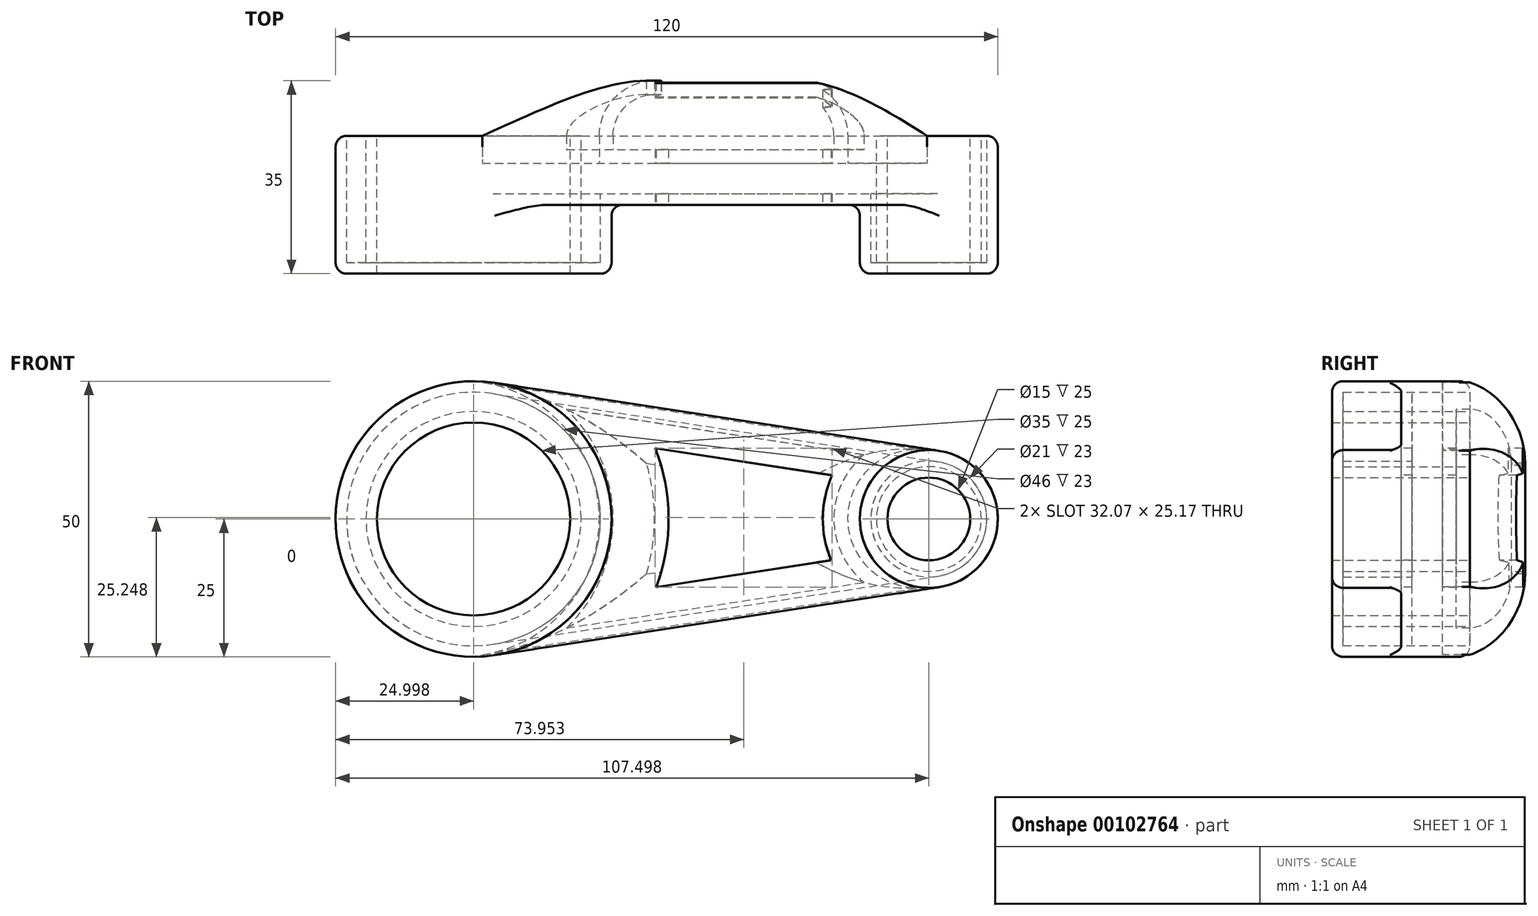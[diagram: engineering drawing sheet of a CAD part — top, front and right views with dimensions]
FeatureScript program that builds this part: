
annotation { "Feature Type Name" : "Feature", "Feature Type Description" : "" }
export const myFeature = defineFeature(function(context is Context, id is Id, definition is map)
    precondition{}
    {
        {
            var Q0;
            Q0=qCreatedBy(makeId("Front.planeOp"),FACE);
            var sketch = newSketch(context, id + "F0", { "sketchPlane" : qUnion([Q0])});
            skLineSegment(sketch, "E0", {"start": v(-63.64, 0) * mm, "end": v(56.36, 0) * mm, "construction": true});
            skLineSegment(sketch, "E1", {"start": v(0, 60.43) * mm, "end": v(0, -61.57) * mm, "construction": true});
            skCircle(sketch, "E2", {"center": v(-38.64, 0) * mm, "radius": 25 * mm});
            skCircle(sketch, "E3", {"center": v(43.86, 0) * mm, "radius": 12.5 * mm});
            skLineSegment(sketch, "E4", {"start": v(-34.85, -24.71) * mm, "end": v(45.75, -12.36) * mm});
            skLineSegment(sketch, "E5", {"start": v(-34.85, 24.71) * mm, "end": v(45.75, 12.36) * mm});
            skCircle(sketch, "E6", {"center": v(-38.64, 0) * mm, "radius": 17.5 * mm});
            skCircle(sketch, "E7", {"center": v(43.86, 0) * mm, "radius": 7.5 * mm});
            skSolve(sketch);
        }
        {
            var Q0;
            {var subQ0=sQuery(id+"F0.wireOp",EDGE,"E4");Q0=makeQuery(id+"F0.imprint","IMPRINT",FACE,{"disambiguationData":[TD([[makeQuery(id+"F0.imprint","IMPRINT",EDGE,{"derivedFrom":subQ0}),1.0]])]});}
            var Q1;
            Q1=makeQuery(id+"F0.imprint","IMPRINT",FACE,{"disambiguationData":[TD([[makeQuery(id+"F0.imprint","IMPRINT",EDGE,{"derivedFrom":sQuery(id+"F0.wireOp",EDGE,"E6")}),1.0]])]});
            var Q2;
            Q2=makeQuery(id+"F0.imprint","IMPRINT",FACE,{"disambiguationData":[TD([[makeQuery(id+"F0.imprint","IMPRINT",EDGE,{"derivedFrom":sQuery(id+"F0.wireOp",EDGE,"E6")}),-1.0]])]});
            var Q3;
            Q3=makeQuery(id+"F0.imprint","IMPRINT",FACE,{"disambiguationData":[TD([[makeQuery(id+"F0.imprint","IMPRINT",EDGE,{"derivedFrom":sQuery(id+"F0.wireOp",EDGE,"E7")}),-1.0]])]});
            var Q4;
            Q4=makeQuery(id+"F0.imprint","IMPRINT",FACE,{"disambiguationData":[TD([[makeQuery(id+"F0.imprint","IMPRINT",EDGE,{"derivedFrom":sQuery(id+"F0.wireOp",EDGE,"E7")}),1.0]])]});
            extrude(context, id + "F6", {"entities" : qUnion([Q0, Q1, Q2, Q3, Q4]), "endBound" : BoundingType.SYMMETRIC, "depth" : 25 * mm});
        }
        {
            var Q0;
            {var subQ0=sQuery(id+"F0.wireOp",EDGE,"E4");Q0=makeQuery(id+"F0.imprint","IMPRINT",FACE,{"disambiguationData":[TD([[makeQuery(id+"F0.imprint","IMPRINT",EDGE,{"derivedFrom":subQ0}),1.0]])]});}
            extrude(context, id + "F7", {"entities" : qUnion([Q0]), "depth" : 25 * mm});
        }
        {
            var Q0;
            Q0=makeQuery(id+"F7.opExtrude","SWEPT_BODY",BODY,{"disambiguationData":[OSD([sQuery(id+"F0.wireOp",EDGE,"E2"),sQuery(id+"F0.wireOp",EDGE,"E3"),sQuery(id+"F0.wireOp",EDGE,"E4"),sQuery(id+"F0.wireOp",EDGE,"E5")])]});
            var Q1;
            Q1=makeQuery(id+"F6.opExtrude","SWEPT_BODY",BODY,{"disambiguationData":[OSD([sQuery(id+"F0.wireOp",EDGE,"E2"),sQuery(id+"F0.wireOp",EDGE,"E3"),sQuery(id+"F0.wireOp",EDGE,"E4"),sQuery(id+"F0.wireOp",EDGE,"E5")])]});
            booleanBodies(context, id + "F8", {"operationType" : BooleanOperationType.INTERSECTION, "tools" : qUnion([Q0, Q1])});
        }
        {
            var Q0;
            Q0=makeQuery(id+"F0.imprint","IMPRINT",FACE,{"disambiguationData":[TD([[makeQuery(id+"F0.imprint","IMPRINT",EDGE,{"derivedFrom":sQuery(id+"F0.wireOp",EDGE,"E7")}),-1.0]])]});
            extrude(context, id + "F9", {"entities" : qUnion([Q0]), "operationType" : NewBodyOperationType.ADD, "depth" : 25 * mm});
        }
        {
            var Q0;
            Q0=makeQuery(id+"F0.imprint","IMPRINT",FACE,{"disambiguationData":[TD([[makeQuery(id+"F0.imprint","IMPRINT",EDGE,{"derivedFrom":sQuery(id+"F0.wireOp",EDGE,"E6")}),-1.0]])]});
            extrude(context, id + "F10", {"entities" : qUnion([Q0]), "operationType" : NewBodyOperationType.ADD, "depth" : 25 * mm});
        }
        {
            var Q0;
            Q0=qCreatedBy(makeId("Front.planeOp"),FACE);
            cPlane(context, id + "F1", {"entities" : qUnion([Q0]), "cplaneType" : CPlaneType.OFFSET, "offset" : 5 * mm, "width" : 150 * mm, "height" : 150 * mm});
        }
        {
            var Q0;
            Q0=qCreatedBy(id+"F1.planeOp",FACE);
            var sketch = newSketch(context, id + "F2", { "sketchPlane" : qUnion([Q0])});
            skLineSegment(sketch, "E8", {"start": v(-65.85, 0.07) * mm, "end": v(54.15, 0.07) * mm, "construction": true});
            skLineSegment(sketch, "E9", {"start": v(-2.21, 60.5) * mm, "end": v(-2.21, -61.5) * mm, "construction": true});
            skCircle(sketch, "E10", {"center": v(-40.85, 0.07) * mm, "radius": 25 * mm});
            skCircle(sketch, "E11", {"center": v(41.65, 0.07) * mm, "radius": 12.5 * mm});
            skLineSegment(sketch, "E12", {"start": v(-37.07, -24.64) * mm, "end": v(43.54, -12.28) * mm});
            skLineSegment(sketch, "E13", {"start": v(-37.07, 24.78) * mm, "end": v(43.54, 12.43) * mm});
            skCircle(sketch, "E14", {"center": v(-40.85, 0.07) * mm, "radius": 17.5 * mm});
            skCircle(sketch, "E15", {"center": v(41.65, 0.07) * mm, "radius": 7.5 * mm});
            skSolve(sketch);
        }
        {
            var Q0;
            {var subQ0=sQuery(id+"F2.wireOp",EDGE,"E12");Q0=makeQuery(id+"F2.imprint","IMPRINT",FACE,{"disambiguationData":[TD([[makeQuery(id+"F2.imprint","IMPRINT",EDGE,{"derivedFrom":subQ0}),1.0]])]});}
            extrude(context, id + "F3", {"entities" : qUnion([Q0]), "oppositeDirection" : true, "depth" : 15 * mm});
        }
        {
            var Q0;
            Q0=makeQuery(id+"F3.opExtrude","CAP_EDGE",EDGE,{"disambiguationData":[OSD([sQuery(id+"F2.wireOp",EDGE,"E11")])],"isStart":false});
            var Q1;
            Q1=makeQuery(id+"F3.opExtrude","CAP_EDGE",EDGE,{"disambiguationData":[OSD([sQuery(id+"F2.wireOp",EDGE,"E10")])],"isStart":false});
            var Q2;
            Q2=makeQuery(id+"F3.opExtrude","CAP_EDGE",EDGE,{"disambiguationData":[OSD([sQuery(id+"F2.wireOp",EDGE,"E13")])],"isStart":false});
            var Q3;
            Q3=makeQuery(id+"F3.opExtrude","CAP_EDGE",EDGE,{"disambiguationData":[OSD([sQuery(id+"F2.wireOp",EDGE,"E12")])],"isStart":false});
            fillet(context, id + "F11", {"entities" : qUnion([Q0, Q1, Q2, Q3]), "radius" : 10 * mm, "tangentPropagation" : true, "allowEdgeOverflow" : false});
        }
        {
            var Q0;
            Q0=makeQuery(id+"F3.opExtrude","CAP_FACE",FACE,{"disambiguationData":[OSD([sQuery(id+"F2.wireOp",EDGE,"E10"),sQuery(id+"F2.wireOp",EDGE,"E11"),sQuery(id+"F2.wireOp",EDGE,"E12"),sQuery(id+"F2.wireOp",EDGE,"E13")])],"isStart":false});
            shell(context, id + "F12", {"entities" : qUnion([Q0]), "thickness" : 2.5 * mm});
        }
        {
            var Q0;
            {var subQ0=sQuery(id+"F0.wireOp",EDGE,"E2");var subQ1=sQuery(id+"F0.wireOp",EDGE,"E3");Q0=makeQuery(id+"F10.boolean.opBoolean","MERGE",FACE,{"derivedFrom":[makeQuery(id+"F9.boolean.opBoolean","MERGE",FACE,{"derivedFrom":[makeQuery(id+"F7.opExtrude","CAP_FACE",FACE,{"disambiguationData":[OSD([subQ0,subQ1,sQuery(id+"F0.wireOp",EDGE,"E4"),sQuery(id+"F0.wireOp",EDGE,"E5")])],"isStart":true}),makeQuery(id+"F9.opExtrude","CAP_FACE",FACE,{"disambiguationData":[OSD([subQ1,sQuery(id+"F0.wireOp",EDGE,"E7")])],"isStart":true})]}),makeQuery(id+"F10.opExtrude","CAP_FACE",FACE,{"disambiguationData":[OSD([subQ0,sQuery(id+"F0.wireOp",EDGE,"E6")])],"isStart":true})]});}
            shell(context, id + "F13", {"entities" : qUnion([Q0]), "thickness" : 2 * mm});
        }
        {
            var Q0;
            {var subQ0=sQuery(id+"F0.wireOp",EDGE,"E2");Q0=makeQuery(id+"F8.opBoolean","INTERSECT",EDGE,{"derivedFrom":[makeQuery(id+"F6.opExtrude","CAP_FACE",FACE,{"disambiguationData":[OSD([subQ0,sQuery(id+"F0.wireOp",EDGE,"E3"),sQuery(id+"F0.wireOp",EDGE,"E4"),sQuery(id+"F0.wireOp",EDGE,"E5")])],"isStart":false}),makeQuery(id+"F7.opExtrude","SWEPT_FACE",FACE,{"disambiguationData":[OSD([subQ0])]})]});}
            var Q1;
            Q1=makeQuery(id+"F9.opExtrude","SWEPT_FACE",FACE,{"disambiguationData":[OSD([sQuery(id+"F0.wireOp",EDGE,"E3")])]});
            var Q2;
            Q2=makeQuery(id+"F10.opExtrude","SWEPT_FACE",FACE,{"disambiguationData":[OSD([sQuery(id+"F0.wireOp",EDGE,"E2")])]});
            var Q3;
            Q3=makeQuery(id+"F6.opExtrude","CAP_EDGE",EDGE,{"disambiguationData":[OSD([sQuery(id+"F0.wireOp",EDGE,"E4")])],"isStart":false});
            var Q4;
            Q4=makeQuery(id+"F6.opExtrude","CAP_EDGE",EDGE,{"disambiguationData":[OSD([sQuery(id+"F0.wireOp",EDGE,"E5")])],"isStart":false});
            fillet(context, id + "F4", {"entities" : qUnion([Q0, Q1, Q2, Q3, Q4]), "radius" : 2 * mm, "tangentPropagation" : true, "allowEdgeOverflow" : false});
        }
        {
            var Q0;
            Q0=makeQuery(id+"F6.opExtrude","CAP_FACE",FACE,{"disambiguationData":[OSD([sQuery(id+"F0.wireOp",EDGE,"E2"),sQuery(id+"F0.wireOp",EDGE,"E3"),sQuery(id+"F0.wireOp",EDGE,"E4"),sQuery(id+"F0.wireOp",EDGE,"E5")])],"isStart":false});
            var sketch = newSketch(context, id + "F14", { "sketchPlane" : qUnion([Q0])});
            skArc(sketch, "E16", {"start": v(-5.53, -12.34) * mm, "mid": v(-3.3, 0.27) * mm, "end": v(-5.72, 12.84) * mm});
            skArc(sketch, "E17", {"start": v(26.35, 7.92) * mm, "mid": v(24.64, 0.24) * mm, "end": v(26.15, -7.48) * mm});
            skLineSegment(sketch, "E18", {"start": v(-5.72, 12.84) * mm, "end": v(26.35, 7.92) * mm});
            skLineSegment(sketch, "E19", {"start": v(-5.53, -12.34) * mm, "end": v(26.15, -7.48) * mm});
            skSolve(sketch);
        }
        {
            var Q0;
            Q0=makeQuery(id+"F14.imprint","IMPRINT",FACE,{"disambiguationData":[TD([[makeQuery(id+"F14.imprint","IMPRINT",EDGE,{"derivedFrom":sQuery(id+"F14.wireOp",EDGE,"E16")}),-1.0]])]});
            extrude(context, id + "F5", {"entities" : qUnion([Q0]), "operationType" : NewBodyOperationType.REMOVE, "oppositeDirection" : true, "depth" : 50 * mm});
        }
    });
